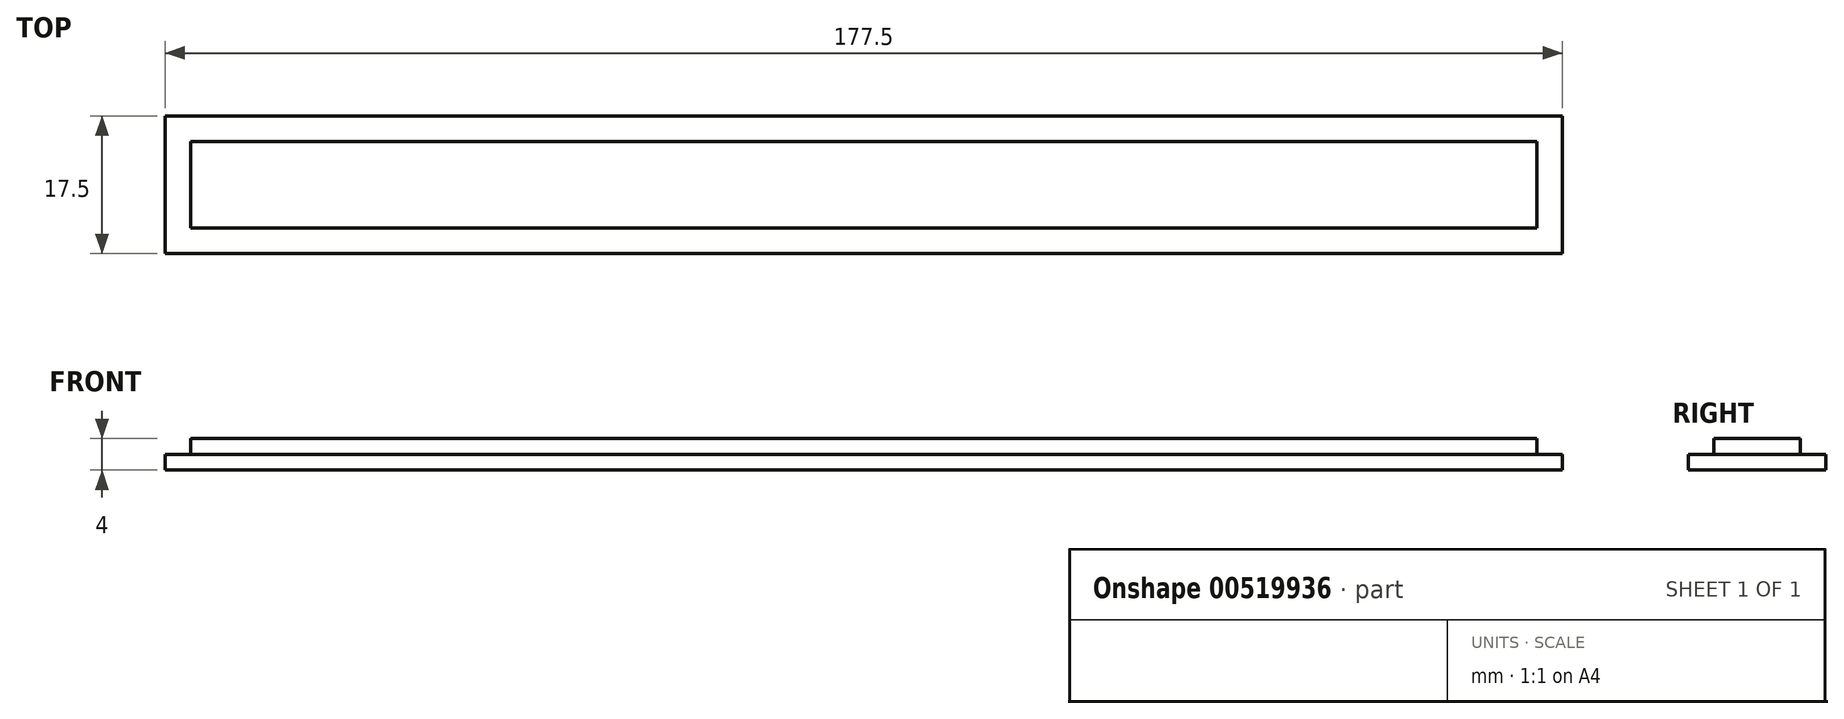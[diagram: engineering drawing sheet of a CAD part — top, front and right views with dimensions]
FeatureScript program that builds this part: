
annotation { "Feature Type Name" : "Feature", "Feature Type Description" : "" }
export const myFeature = defineFeature(function(context is Context, id is Id, definition is map)
    precondition{}
    {
        {
            var Q0;
            Q0=qCreatedBy(makeId("Top.planeOp"),FACE);
            var sketch = newSketch(context, id + "F0", { "sketchPlane" : qUnion([Q0])});
            skLineSegment(sketch, "E0.bottom", {"start": v(0, 0) * mm, "end": v(177.5, 0) * mm});
            skLineSegment(sketch, "E0.top", {"start": v(0, -17.5) * mm, "end": v(177.5, -17.5) * mm});
            skLineSegment(sketch, "E0.left", {"start": v(0, 0) * mm, "end": v(0, -17.5) * mm});
            skLineSegment(sketch, "E0.right", {"start": v(177.5, 0) * mm, "end": v(177.5, -17.5) * mm});
            skSolve(sketch);
        }
        {
            var Q0;
            Q0 = qSketchRegion(id + "F0", true);
            extrude(context, id + "F1", {"entities" : qUnion([Q0]), "depth" : 2 * mm, "offsetDistance" : 25 * mm});
        }
        {
            var Q0;
            Q0=makeQuery(id+"F1.opExtrude","CAP_FACE",FACE,{"disambiguationData":[OSD([sQuery(id+"F0.wireOp",EDGE,"E0.bottom"),sQuery(id+"F0.wireOp",EDGE,"E0.top"),sQuery(id+"F0.wireOp",EDGE,"E0.left"),sQuery(id+"F0.wireOp",EDGE,"E0.right")])],"isStart":false});
            var sketch = newSketch(context, id + "F2", { "sketchPlane" : qUnion([Q0])});
            skLineSegment(sketch, "E1", {"start": v(0, -8.75) * mm, "end": v(3.25, -8.75) * mm, "construction": true});
            skLineSegment(sketch, "E2", {"start": v(88.75, 0) * mm, "end": v(88.75, -3.25) * mm, "construction": true});
            skLineSegment(sketch, "E3.bottom", {"start": v(3.25, -3.25) * mm, "end": v(174.25, -3.25) * mm});
            skLineSegment(sketch, "E3.top", {"start": v(3.25, -14.25) * mm, "end": v(174.25, -14.25) * mm});
            skLineSegment(sketch, "E3.left", {"start": v(3.25, -3.25) * mm, "end": v(3.25, -14.25) * mm});
            skLineSegment(sketch, "E3.right", {"start": v(174.25, -3.25) * mm, "end": v(174.25, -14.25) * mm});
            skSolve(sketch);
        }
        {
            var Q0;
            Q0 = qSketchRegion(id + "F2", true);
            var Q1;
            Q1=sQuery(id+"F2.wireOp",EDGE,"E3.top");
            extrude(context, id + "F3", {"entities" : qUnion([Q0]), "operationType" : NewBodyOperationType.ADD, "surfaceEntities" : qUnion([Q1]), "depth" : 2 * mm, "offsetDistance" : 25 * mm});
        }
    });
